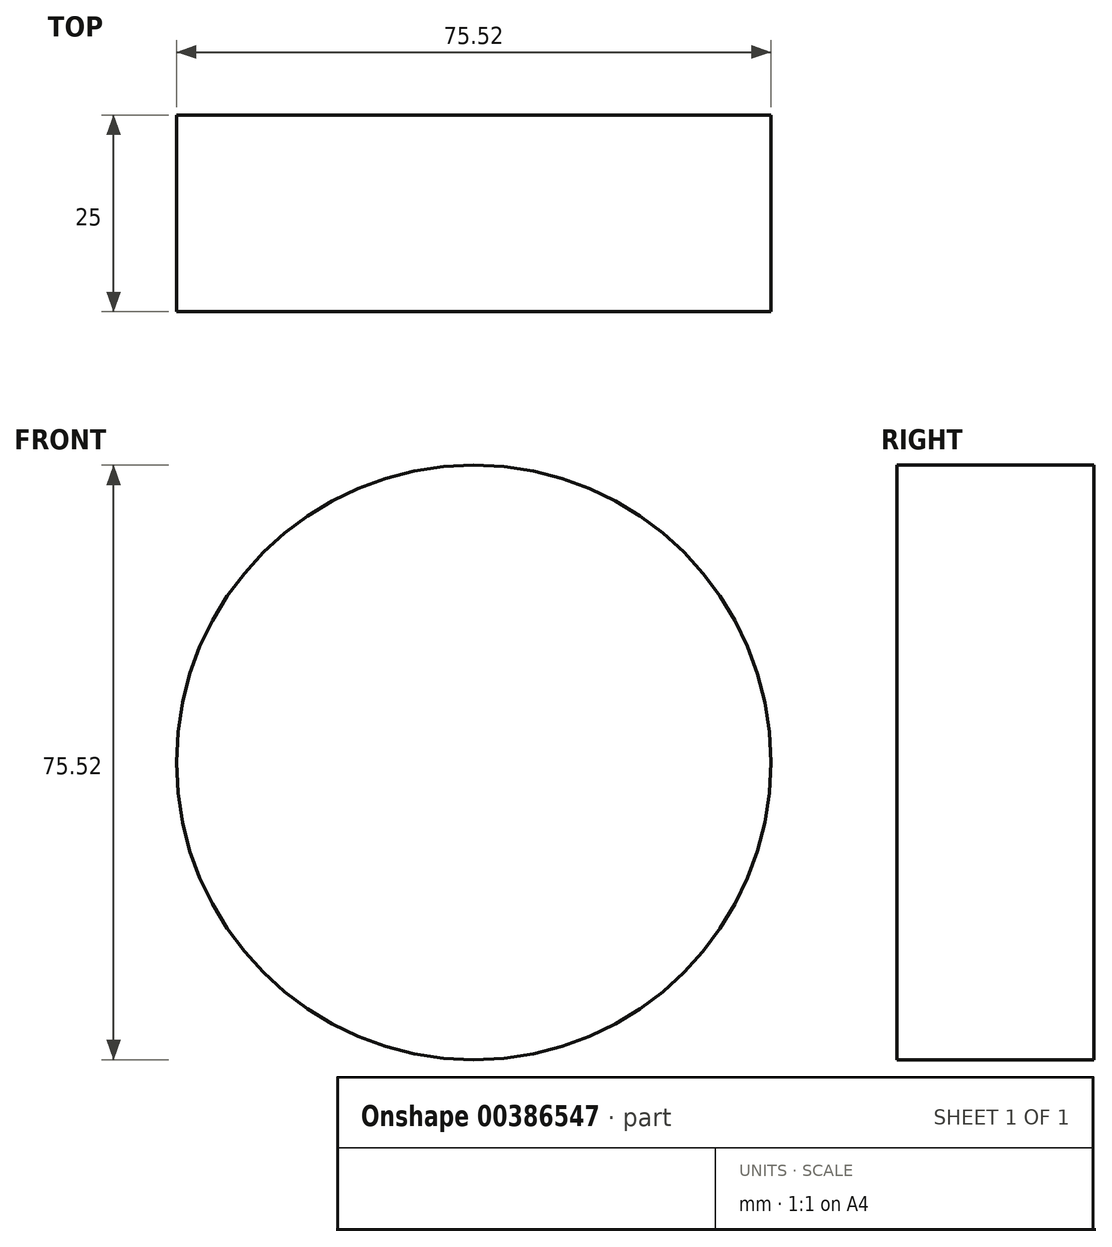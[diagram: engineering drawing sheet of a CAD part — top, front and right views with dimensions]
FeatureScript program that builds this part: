
annotation { "Feature Type Name" : "Feature", "Feature Type Description" : "" }
export const myFeature = defineFeature(function(context is Context, id is Id, definition is map)
    precondition{}
    {
        {
            var Q0;
            Q0=qCreatedBy(makeId("Front.planeOp"),FACE);
            var sketch = newSketch(context, id + "F0", { "sketchPlane" : qUnion([Q0])});
            skCircle(sketch, "E0", {"center": v(0, 0) * mm, "radius": 37.76 * mm});
            skSolve(sketch);
        }
        {
            var Q0;
            Q0 = qSketchRegion(id + "F0", true);
            extrude(context, id + "F1", {"entities" : qUnion([Q0]), "depth" : 25 * mm});
        }
    });
